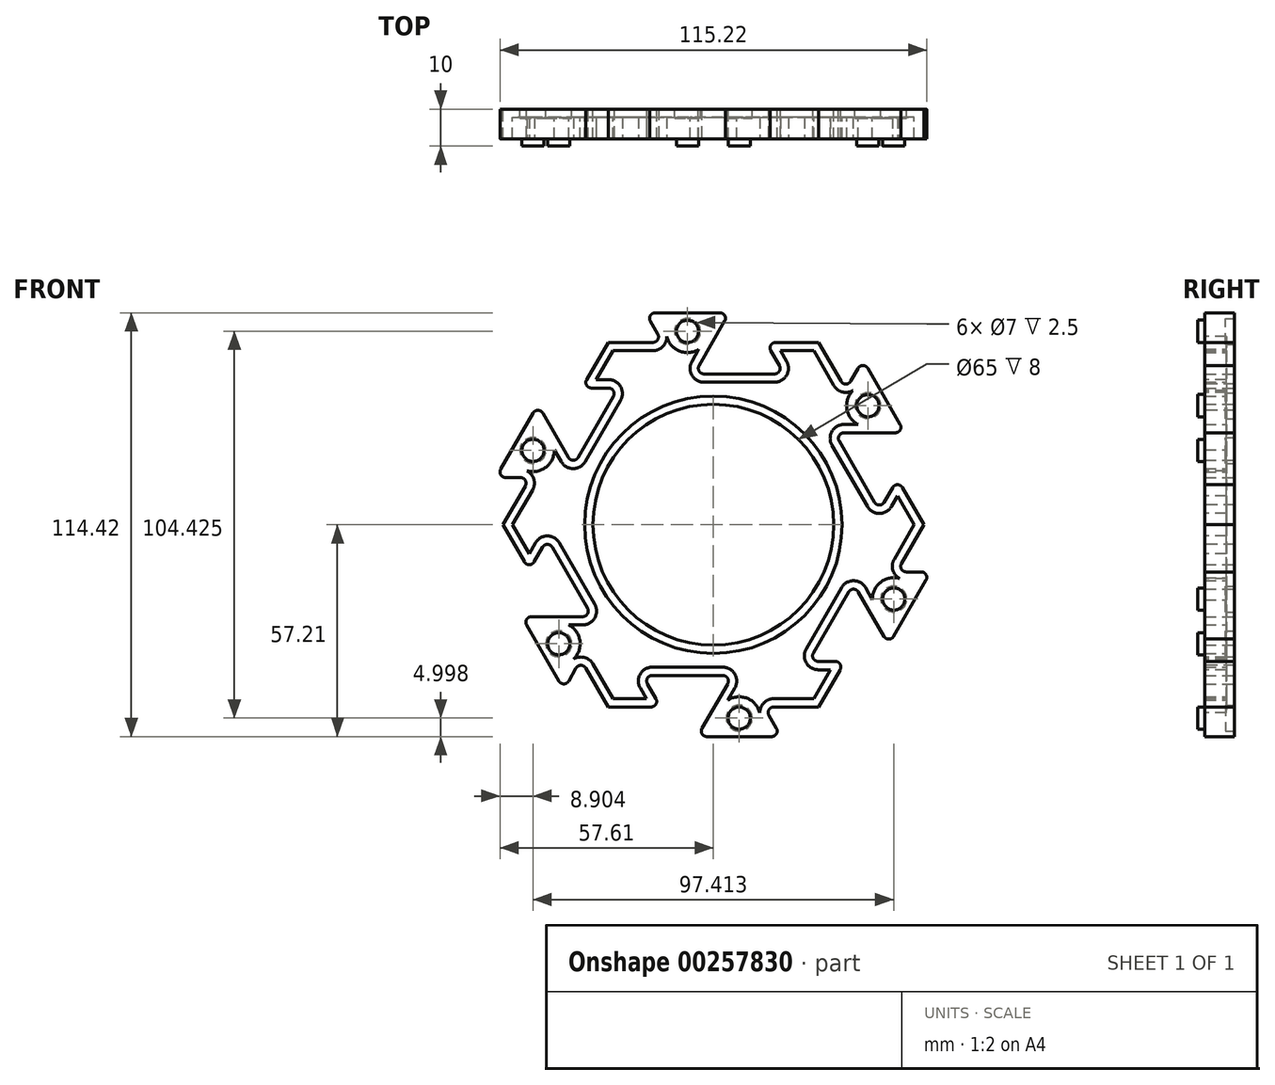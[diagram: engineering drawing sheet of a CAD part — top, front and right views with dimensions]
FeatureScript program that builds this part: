
annotation { "Feature Type Name" : "Feature", "Feature Type Description" : "" }
export const myFeature = defineFeature(function(context is Context, id is Id, definition is map)
    precondition{}
    {
        {
            var Q0;
            Q0=qCreatedBy(makeId("Front.planeOp"),FACE);
            var sketch = newSketch(context, id + "F0", { "sketchPlane" : qUnion([Q0])});
            skLineSegment(sketch, "E0.0", {"start": v(-28.41, 49.21) * mm, "end": v(-13.7, 49.21) * mm});
            skPoint(sketch, "E0.0.midPoint", {"position": v(0, 49.21) * mm});
            skPoint(sketch, "E1", {"position": v(-13.7, 49.21) * mm});
            skPoint(sketch, "E2", {"position": v(-0.25, 49.21) * mm});
            skPoint(sketch, "E3", {"position": v(14.2, 49.21) * mm});
            skPoint(sketch, "E4", {"position": v(-5.16, 40.71) * mm});
            skLineSegment(sketch, "E5", {"start": v(14.2, 49.21) * mm, "end": v(19.11, 40.71) * mm, "construction": true});
            skLineSegment(sketch, "E6", {"start": v(-13.7, 49.21) * mm, "end": v(-18.33, 57.21) * mm, "construction": true});
            skPoint(sketch, "E7", {"position": v(-18.33, 57.21) * mm});
            skPoint(sketch, "E8", {"position": v(4.37, 57.21) * mm});
            skPoint(sketch, "E9", {"position": v(19.11, 40.71) * mm});
            skLineSegment(sketch, "E10.trimOffspring", {"start": v(-0.25, 49.21) * mm, "end": v(0, 49.21) * mm});
            skLineSegment(sketch, "E11.trimOffspring", {"start": v(14.2, 49.21) * mm, "end": v(28.41, 49.21) * mm});
            skLineSegment(sketch, "E12", {"start": v(-13.7, 49.21) * mm, "end": v(-18.33, 57.21) * mm});
            skLineSegment(sketch, "E13", {"start": v(4.37, 57.21) * mm, "end": v(-0.25, 49.21) * mm});
            skLineSegment(sketch, "E14", {"start": v(-5.16, 40.71) * mm, "end": v(-0.25, 49.21) * mm});
            skLineSegment(sketch, "E15", {"start": v(-5.16, 40.71) * mm, "end": v(19.11, 40.71) * mm});
            skLineSegment(sketch, "E16", {"start": v(19.11, 40.71) * mm, "end": v(14.2, 49.21) * mm});
            skLineSegment(sketch, "E17", {"start": v(-18.33, 57.21) * mm, "end": v(4.37, 57.21) * mm});
            skLineSegment(sketch, "E18", {"start": v(-28.41, 49.21) * mm, "end": v(-16.75, 29.01) * mm});
            skLineSegment(sketch, "E19", {"start": v(16.75, 29.01) * mm, "end": v(28.41, 49.21) * mm});
            skPoint(sketch, "E20", {"position": v(0, 0) * mm});
            skLineSegment(sketch, "E21", {"start": v(-13.7, 49.21) * mm, "end": v(-0.25, 49.21) * mm, "construction": true});
            skArc(sketch, "E22", {"start": v(16.25, 28.15) * mm, "mid": v(0, 32.5) * mm, "end": v(-16.25, 28.15) * mm});
            skPoint(sketch, "E23", {"position": v(-16.75, 29.01) * mm});
            skPoint(sketch, "E24", {"position": v(14.65, 29.01) * mm});
            skLineSegment(sketch, "E25", {"start": v(-16.75, 29.01) * mm, "end": v(0, 0) * mm, "construction": true});
            skLineSegment(sketch, "E26", {"start": v(0, 0) * mm, "end": v(16.75, 29.01) * mm, "construction": true});
            skLineSegment(sketch, "E27", {"start": v(-16.75, 29.01) * mm, "end": v(-16.25, 28.15) * mm});
            skLineSegment(sketch, "E28", {"start": v(16.75, 29.01) * mm, "end": v(16.25, 28.15) * mm});
            skSolve(sketch);
        }
        {
            var Q0;
            Q0=qCreatedBy(makeId("Right.planeOp"),FACE);
            var sketch = newSketch(context, id + "F1", { "sketchPlane" : qUnion([Q0])});
            skLineSegment(sketch, "E29", {"start": v(0, 0) * mm, "end": v(-16.4, 0) * mm, "construction": true});
            skSolve(sketch);
        }
        {
            var Q0;
            Q0=makeQuery(id+"F0.imprint","IMPRINT",FACE,{"disambiguationData":[TD([[makeQuery(id+"F0.imprint","IMPRINT",EDGE,{"derivedFrom":sQuery(id+"F0.wireOp",EDGE,"E0.0")}),-1.0]])]});
            extrude(context, id + "F2", {"entities" : qUnion([Q0]), "depth" : 8 * mm});
        }
        {
            var Q0;
            {var subQ0=makeQuery(id+"F2.opExtrude","CAP_FACE",FACE,{"disambiguationData":[OSD([sQuery(id+"F0.wireOp",EDGE,"Ghvy13B3-qNFz-JgCi-f515-eY6BPN7KZuCC"),sQuery(id+"F0.wireOp",EDGE,"E0.0"),sQuery(id+"F0.wireOp",EDGE,"E11.trimOffspring"),sQuery(id+"F0.wireOp",EDGE,"E12"),sQuery(id+"F0.wireOp",EDGE,"E13"),sQuery(id+"F0.wireOp",EDGE,"E14"),sQuery(id+"F0.wireOp",EDGE,"E15"),sQuery(id+"F0.wireOp",EDGE,"E16"),sQuery(id+"F0.wireOp",EDGE,"E17"),sQuery(id+"F0.wireOp",EDGE,"E18"),sQuery(id+"F0.wireOp",EDGE,"E19")])],"isStart":false});Q0=makeQuery(id+"F12.opBoolean","MERGE",FACE,{"derivedFrom":[subQ0,makeQuery(id+"F7.opPattern","COPY",FACE,{"derivedFrom":subQ0,"instanceName":"1"}),makeQuery(id+"F8.opPattern","COPY",FACE,{"derivedFrom":subQ0,"instanceName":"1"}),makeQuery(id+"F9.opPattern","COPY",FACE,{"derivedFrom":subQ0,"instanceName":"1"}),makeQuery(id+"F10.opPattern","COPY",FACE,{"derivedFrom":subQ0,"instanceName":"1"}),makeQuery(id+"F11.opPattern","COPY",FACE,{"derivedFrom":subQ0,"instanceName":"1"})]});}
            var sketch = newSketch(context, id + "F3", { "sketchPlane" : qUnion([Q0])});
            skLineSegment(sketch, "E30", {"start": v(-13.65, 49.21) * mm, "end": v(-0.25, 49.21) * mm, "construction": true});
            skLineSegment(sketch, "E31", {"start": v(-6.98, 57.21) * mm, "end": v(-6.98, 49.21) * mm, "construction": true});
            skPoint(sketch, "E32", {"position": v(-6.98, 52.21) * mm});
            skCircle(sketch, "E33", {"center": v(-6.98, 52.21) * mm, "radius": 3 * mm});
            skSolve(sketch);
        }
        {
            var Q0;
            Q0=makeQuery(id+"F3.imprint","IMPRINT",FACE,{"disambiguationData":[TD([[makeQuery(id+"F3.imprint","IMPRINT",EDGE,{"derivedFrom":sQuery(id+"F3.wireOp",EDGE,"E33")}),1.0]])]});
            extrude(context, id + "F4", {"entities" : qUnion([Q0]), "operationType" : NewBodyOperationType.ADD, "depth" : 2 * mm});
        }
        {
            var Q0;
            Q0=qCreatedBy(makeId("Front.planeOp"),FACE);
            var sketch = newSketch(context, id + "F5", { "sketchPlane" : qUnion([Q0])});
            skPoint(sketch, "E34.0", {"position": v(-6.98, 52.21) * mm});
            skCircle(sketch, "E35", {"center": v(-6.98, 52.21) * mm, "radius": 3.5 * mm});
            skSolve(sketch);
        }
        {
            var Q0;
            Q0=makeQuery(id+"F5.imprint","IMPRINT",FACE,{"disambiguationData":[TD([[makeQuery(id+"F5.imprint","IMPRINT",EDGE,{"derivedFrom":sQuery(id+"F5.wireOp",EDGE,"E35")}),1.0]])]});
            var Q1;
            Q1=sQuery(id+"F5.wireOp",EDGE,"E35");
            extrude(context, id + "F6", {"entities" : qUnion([Q0]), "operationType" : NewBodyOperationType.REMOVE, "surfaceEntities" : qUnion([Q1]), "depth" : 2.5 * mm});
        }
        {
            var Q0;
            Q0=makeQuery(id+"F2.opExtrude","SWEPT_BODY",BODY,{"disambiguationData":[OSD([sQuery(id+"F0.wireOp",EDGE,"Ghvy13B3-qNFz-JgCi-f515-eY6BPN7KZuCC"),sQuery(id+"F0.wireOp",EDGE,"E0.0"),sQuery(id+"F0.wireOp",EDGE,"E11.trimOffspring"),sQuery(id+"F0.wireOp",EDGE,"E12"),sQuery(id+"F0.wireOp",EDGE,"E13"),sQuery(id+"F0.wireOp",EDGE,"E14"),sQuery(id+"F0.wireOp",EDGE,"E15"),sQuery(id+"F0.wireOp",EDGE,"E16"),sQuery(id+"F0.wireOp",EDGE,"E17"),sQuery(id+"F0.wireOp",EDGE,"E18"),sQuery(id+"F0.wireOp",EDGE,"E19")])]});
            var Q1;
            Q1=sQuery(id+"F1.wireOp",EDGE,"E29");
            transform(context, id + "F7", {"entities" : qUnion([Q0]), "transformType" : TransformType.ROTATION, "transformAxis" : qUnion([Q1]), "angle" : 60 * degree, "makeCopy" : true});
        }
        {
            var Q0;
            Q0=makeQuery(id+"F2.opExtrude","SWEPT_BODY",BODY,{"disambiguationData":[OSD([sQuery(id+"F0.wireOp",EDGE,"Ghvy13B3-qNFz-JgCi-f515-eY6BPN7KZuCC"),sQuery(id+"F0.wireOp",EDGE,"E0.0"),sQuery(id+"F0.wireOp",EDGE,"E11.trimOffspring"),sQuery(id+"F0.wireOp",EDGE,"E12"),sQuery(id+"F0.wireOp",EDGE,"E13"),sQuery(id+"F0.wireOp",EDGE,"E14"),sQuery(id+"F0.wireOp",EDGE,"E15"),sQuery(id+"F0.wireOp",EDGE,"E16"),sQuery(id+"F0.wireOp",EDGE,"E17"),sQuery(id+"F0.wireOp",EDGE,"E18"),sQuery(id+"F0.wireOp",EDGE,"E19")])]});
            var Q1;
            Q1=sQuery(id+"F1.wireOp",EDGE,"E29");
            transform(context, id + "F8", {"entities" : qUnion([Q0]), "transformType" : TransformType.ROTATION, "transformAxis" : qUnion([Q1]), "angle" : 120 * degree, "makeCopy" : true});
        }
        {
            var Q0;
            Q0=makeQuery(id+"F2.opExtrude","SWEPT_BODY",BODY,{"disambiguationData":[OSD([sQuery(id+"F0.wireOp",EDGE,"Ghvy13B3-qNFz-JgCi-f515-eY6BPN7KZuCC"),sQuery(id+"F0.wireOp",EDGE,"E0.0"),sQuery(id+"F0.wireOp",EDGE,"E11.trimOffspring"),sQuery(id+"F0.wireOp",EDGE,"E12"),sQuery(id+"F0.wireOp",EDGE,"E13"),sQuery(id+"F0.wireOp",EDGE,"E14"),sQuery(id+"F0.wireOp",EDGE,"E15"),sQuery(id+"F0.wireOp",EDGE,"E16"),sQuery(id+"F0.wireOp",EDGE,"E17"),sQuery(id+"F0.wireOp",EDGE,"E18"),sQuery(id+"F0.wireOp",EDGE,"E19")])]});
            var Q1;
            Q1=sQuery(id+"F1.wireOp",EDGE,"E29");
            transform(context, id + "F9", {"entities" : qUnion([Q0]), "transformType" : TransformType.ROTATION, "transformAxis" : qUnion([Q1]), "angle" : 180 * degree, "makeCopy" : true});
        }
        {
            var Q0;
            Q0=makeQuery(id+"F2.opExtrude","SWEPT_BODY",BODY,{"disambiguationData":[OSD([sQuery(id+"F0.wireOp",EDGE,"Ghvy13B3-qNFz-JgCi-f515-eY6BPN7KZuCC"),sQuery(id+"F0.wireOp",EDGE,"E0.0"),sQuery(id+"F0.wireOp",EDGE,"E11.trimOffspring"),sQuery(id+"F0.wireOp",EDGE,"E12"),sQuery(id+"F0.wireOp",EDGE,"E13"),sQuery(id+"F0.wireOp",EDGE,"E14"),sQuery(id+"F0.wireOp",EDGE,"E15"),sQuery(id+"F0.wireOp",EDGE,"E16"),sQuery(id+"F0.wireOp",EDGE,"E17"),sQuery(id+"F0.wireOp",EDGE,"E18"),sQuery(id+"F0.wireOp",EDGE,"E19")])]});
            var Q1;
            Q1=sQuery(id+"F1.wireOp",EDGE,"E29");
            transform(context, id + "F10", {"entities" : qUnion([Q0]), "transformType" : TransformType.ROTATION, "transformAxis" : qUnion([Q1]), "angle" : 240 * degree, "makeCopy" : true});
        }
        {
            var Q0;
            Q0=makeQuery(id+"F2.opExtrude","SWEPT_BODY",BODY,{"disambiguationData":[OSD([sQuery(id+"F0.wireOp",EDGE,"Ghvy13B3-qNFz-JgCi-f515-eY6BPN7KZuCC"),sQuery(id+"F0.wireOp",EDGE,"E0.0"),sQuery(id+"F0.wireOp",EDGE,"E11.trimOffspring"),sQuery(id+"F0.wireOp",EDGE,"E12"),sQuery(id+"F0.wireOp",EDGE,"E13"),sQuery(id+"F0.wireOp",EDGE,"E14"),sQuery(id+"F0.wireOp",EDGE,"E15"),sQuery(id+"F0.wireOp",EDGE,"E16"),sQuery(id+"F0.wireOp",EDGE,"E17"),sQuery(id+"F0.wireOp",EDGE,"E18"),sQuery(id+"F0.wireOp",EDGE,"E19")])]});
            var Q1;
            Q1=sQuery(id+"F1.wireOp",EDGE,"E29");
            transform(context, id + "F11", {"entities" : qUnion([Q0]), "transformType" : TransformType.ROTATION, "transformAxis" : qUnion([Q1]), "angle" : 300 * degree, "makeCopy" : true});
        }
        {
            var Q0;
            Q0=makeQuery(id+"F2.opExtrude","SWEPT_BODY",BODY,{"disambiguationData":[OSD([sQuery(id+"F0.wireOp",EDGE,"Ghvy13B3-qNFz-JgCi-f515-eY6BPN7KZuCC"),sQuery(id+"F0.wireOp",EDGE,"E0.0"),sQuery(id+"F0.wireOp",EDGE,"E11.trimOffspring"),sQuery(id+"F0.wireOp",EDGE,"E12"),sQuery(id+"F0.wireOp",EDGE,"E13"),sQuery(id+"F0.wireOp",EDGE,"E14"),sQuery(id+"F0.wireOp",EDGE,"E15"),sQuery(id+"F0.wireOp",EDGE,"E16"),sQuery(id+"F0.wireOp",EDGE,"E17"),sQuery(id+"F0.wireOp",EDGE,"E18"),sQuery(id+"F0.wireOp",EDGE,"E19")])]});
            var Q1;
            Q1=makeQuery(id+"F7.opPattern","COPY",BODY,{"derivedFrom":makeQuery(id+"F2.opExtrude","SWEPT_BODY",BODY,{"disambiguationData":[OSD([sQuery(id+"F0.wireOp",EDGE,"Ghvy13B3-qNFz-JgCi-f515-eY6BPN7KZuCC"),sQuery(id+"F0.wireOp",EDGE,"E0.0"),sQuery(id+"F0.wireOp",EDGE,"E11.trimOffspring"),sQuery(id+"F0.wireOp",EDGE,"E12"),sQuery(id+"F0.wireOp",EDGE,"E13"),sQuery(id+"F0.wireOp",EDGE,"E14"),sQuery(id+"F0.wireOp",EDGE,"E15"),sQuery(id+"F0.wireOp",EDGE,"E16"),sQuery(id+"F0.wireOp",EDGE,"E17"),sQuery(id+"F0.wireOp",EDGE,"E18"),sQuery(id+"F0.wireOp",EDGE,"E19")])]}),"instanceName":"1"});
            var Q2;
            Q2=makeQuery(id+"F8.opPattern","COPY",BODY,{"derivedFrom":makeQuery(id+"F2.opExtrude","SWEPT_BODY",BODY,{"disambiguationData":[OSD([sQuery(id+"F0.wireOp",EDGE,"Ghvy13B3-qNFz-JgCi-f515-eY6BPN7KZuCC"),sQuery(id+"F0.wireOp",EDGE,"E0.0"),sQuery(id+"F0.wireOp",EDGE,"E11.trimOffspring"),sQuery(id+"F0.wireOp",EDGE,"E12"),sQuery(id+"F0.wireOp",EDGE,"E13"),sQuery(id+"F0.wireOp",EDGE,"E14"),sQuery(id+"F0.wireOp",EDGE,"E15"),sQuery(id+"F0.wireOp",EDGE,"E16"),sQuery(id+"F0.wireOp",EDGE,"E17"),sQuery(id+"F0.wireOp",EDGE,"E18"),sQuery(id+"F0.wireOp",EDGE,"E19")])]}),"instanceName":"1"});
            var Q3;
            Q3=makeQuery(id+"F9.opPattern","COPY",BODY,{"derivedFrom":makeQuery(id+"F2.opExtrude","SWEPT_BODY",BODY,{"disambiguationData":[OSD([sQuery(id+"F0.wireOp",EDGE,"Ghvy13B3-qNFz-JgCi-f515-eY6BPN7KZuCC"),sQuery(id+"F0.wireOp",EDGE,"E0.0"),sQuery(id+"F0.wireOp",EDGE,"E11.trimOffspring"),sQuery(id+"F0.wireOp",EDGE,"E12"),sQuery(id+"F0.wireOp",EDGE,"E13"),sQuery(id+"F0.wireOp",EDGE,"E14"),sQuery(id+"F0.wireOp",EDGE,"E15"),sQuery(id+"F0.wireOp",EDGE,"E16"),sQuery(id+"F0.wireOp",EDGE,"E17"),sQuery(id+"F0.wireOp",EDGE,"E18"),sQuery(id+"F0.wireOp",EDGE,"E19")])]}),"instanceName":"1"});
            var Q4;
            Q4=makeQuery(id+"F10.opPattern","COPY",BODY,{"derivedFrom":makeQuery(id+"F2.opExtrude","SWEPT_BODY",BODY,{"disambiguationData":[OSD([sQuery(id+"F0.wireOp",EDGE,"Ghvy13B3-qNFz-JgCi-f515-eY6BPN7KZuCC"),sQuery(id+"F0.wireOp",EDGE,"E0.0"),sQuery(id+"F0.wireOp",EDGE,"E11.trimOffspring"),sQuery(id+"F0.wireOp",EDGE,"E12"),sQuery(id+"F0.wireOp",EDGE,"E13"),sQuery(id+"F0.wireOp",EDGE,"E14"),sQuery(id+"F0.wireOp",EDGE,"E15"),sQuery(id+"F0.wireOp",EDGE,"E16"),sQuery(id+"F0.wireOp",EDGE,"E17"),sQuery(id+"F0.wireOp",EDGE,"E18"),sQuery(id+"F0.wireOp",EDGE,"E19")])]}),"instanceName":"1"});
            var Q5;
            Q5=makeQuery(id+"F11.opPattern","COPY",BODY,{"derivedFrom":makeQuery(id+"F2.opExtrude","SWEPT_BODY",BODY,{"disambiguationData":[OSD([sQuery(id+"F0.wireOp",EDGE,"Ghvy13B3-qNFz-JgCi-f515-eY6BPN7KZuCC"),sQuery(id+"F0.wireOp",EDGE,"E0.0"),sQuery(id+"F0.wireOp",EDGE,"E11.trimOffspring"),sQuery(id+"F0.wireOp",EDGE,"E12"),sQuery(id+"F0.wireOp",EDGE,"E13"),sQuery(id+"F0.wireOp",EDGE,"E14"),sQuery(id+"F0.wireOp",EDGE,"E15"),sQuery(id+"F0.wireOp",EDGE,"E16"),sQuery(id+"F0.wireOp",EDGE,"E17"),sQuery(id+"F0.wireOp",EDGE,"E18"),sQuery(id+"F0.wireOp",EDGE,"E19")])]}),"instanceName":"1"});
            booleanBodies(context, id + "F12", {"operationType" : BooleanOperationType.UNION, "tools" : qUnion([Q0, Q1, Q2, Q3, Q4, Q5])});
        }
        {
            var Q0;
            Q0=makeQuery(id+"F7.opPattern","COPY",EDGE,{"derivedFrom":makeQuery(id+"F2.opExtrude","SWEPT_EDGE",EDGE,{"disambiguationData":[OSD([sQuery(id+"F0.wireOp",EDGE,"E11.trimOffspring"),sQuery(id+"F0.wireOp",EDGE,"E16")])]}),"instanceName":"1"});
            var Q1;
            Q1=makeQuery(id+"F7.opPattern","COPY",EDGE,{"derivedFrom":makeQuery(id+"F2.opExtrude","SWEPT_EDGE",EDGE,{"disambiguationData":[OSD([sQuery(id+"F0.wireOp",EDGE,"E13"),sQuery(id+"F0.wireOp",EDGE,"E17")])]}),"instanceName":"1"});
            var Q2;
            Q2=makeQuery(id+"F7.opPattern","COPY",EDGE,{"derivedFrom":makeQuery(id+"F2.opExtrude","SWEPT_EDGE",EDGE,{"disambiguationData":[OSD([sQuery(id+"F0.wireOp",EDGE,"E12"),sQuery(id+"F0.wireOp",EDGE,"E17")])]}),"instanceName":"1"});
            var Q3;
            Q3=makeQuery(id+"F2.opExtrude","SWEPT_EDGE",EDGE,{"disambiguationData":[OSD([sQuery(id+"F0.wireOp",EDGE,"E12"),sQuery(id+"F0.wireOp",EDGE,"E17")])]});
            var Q4;
            Q4=makeQuery(id+"F2.opExtrude","SWEPT_EDGE",EDGE,{"disambiguationData":[OSD([sQuery(id+"F0.wireOp",EDGE,"E11.trimOffspring"),sQuery(id+"F0.wireOp",EDGE,"E16")])]});
            var Q5;
            Q5=makeQuery(id+"F11.opPattern","COPY",EDGE,{"derivedFrom":makeQuery(id+"F2.opExtrude","SWEPT_EDGE",EDGE,{"disambiguationData":[OSD([sQuery(id+"F0.wireOp",EDGE,"E12"),sQuery(id+"F0.wireOp",EDGE,"E17")])]}),"instanceName":"1"});
            var Q6;
            Q6=makeQuery(id+"F11.opPattern","COPY",EDGE,{"derivedFrom":makeQuery(id+"F2.opExtrude","SWEPT_EDGE",EDGE,{"disambiguationData":[OSD([sQuery(id+"F0.wireOp",EDGE,"E11.trimOffspring"),sQuery(id+"F0.wireOp",EDGE,"E16")])]}),"instanceName":"1"});
            var Q7;
            Q7=makeQuery(id+"F10.opPattern","COPY",EDGE,{"derivedFrom":makeQuery(id+"F2.opExtrude","SWEPT_EDGE",EDGE,{"disambiguationData":[OSD([sQuery(id+"F0.wireOp",EDGE,"E13"),sQuery(id+"F0.wireOp",EDGE,"E17")])]}),"instanceName":"1"});
            var Q8;
            Q8=makeQuery(id+"F9.opPattern","COPY",EDGE,{"derivedFrom":makeQuery(id+"F2.opExtrude","SWEPT_EDGE",EDGE,{"disambiguationData":[OSD([sQuery(id+"F0.wireOp",EDGE,"E13"),sQuery(id+"F0.wireOp",EDGE,"E17")])]}),"instanceName":"1"});
            var Q9;
            Q9=makeQuery(id+"F8.opPattern","COPY",EDGE,{"derivedFrom":makeQuery(id+"F2.opExtrude","SWEPT_EDGE",EDGE,{"disambiguationData":[OSD([sQuery(id+"F0.wireOp",EDGE,"E12"),sQuery(id+"F0.wireOp",EDGE,"E17")])]}),"instanceName":"1"});
            var Q10;
            Q10=makeQuery(id+"F8.opPattern","COPY",EDGE,{"derivedFrom":makeQuery(id+"F2.opExtrude","SWEPT_EDGE",EDGE,{"disambiguationData":[OSD([sQuery(id+"F0.wireOp",EDGE,"E13"),sQuery(id+"F0.wireOp",EDGE,"E17")])]}),"instanceName":"1"});
            var Q11;
            Q11=makeQuery(id+"F8.opPattern","COPY",EDGE,{"derivedFrom":makeQuery(id+"F2.opExtrude","SWEPT_EDGE",EDGE,{"disambiguationData":[OSD([sQuery(id+"F0.wireOp",EDGE,"E11.trimOffspring"),sQuery(id+"F0.wireOp",EDGE,"E16")])]}),"instanceName":"1"});
            var Q12;
            Q12=makeQuery(id+"F2.opExtrude","SWEPT_EDGE",EDGE,{"disambiguationData":[OSD([sQuery(id+"F0.wireOp",EDGE,"E13"),sQuery(id+"F0.wireOp",EDGE,"E17")])]});
            var Q13;
            Q13=makeQuery(id+"F11.opPattern","COPY",EDGE,{"derivedFrom":makeQuery(id+"F2.opExtrude","SWEPT_EDGE",EDGE,{"disambiguationData":[OSD([sQuery(id+"F0.wireOp",EDGE,"E13"),sQuery(id+"F0.wireOp",EDGE,"E17")])]}),"instanceName":"1"});
            var Q14;
            Q14=makeQuery(id+"F10.opPattern","COPY",EDGE,{"derivedFrom":makeQuery(id+"F2.opExtrude","SWEPT_EDGE",EDGE,{"disambiguationData":[OSD([sQuery(id+"F0.wireOp",EDGE,"E12"),sQuery(id+"F0.wireOp",EDGE,"E17")])]}),"instanceName":"1"});
            var Q15;
            Q15=makeQuery(id+"F10.opPattern","COPY",EDGE,{"derivedFrom":makeQuery(id+"F2.opExtrude","SWEPT_EDGE",EDGE,{"disambiguationData":[OSD([sQuery(id+"F0.wireOp",EDGE,"E11.trimOffspring"),sQuery(id+"F0.wireOp",EDGE,"E16")])]}),"instanceName":"1"});
            var Q16;
            Q16=makeQuery(id+"F9.opPattern","COPY",EDGE,{"derivedFrom":makeQuery(id+"F2.opExtrude","SWEPT_EDGE",EDGE,{"disambiguationData":[OSD([sQuery(id+"F0.wireOp",EDGE,"E12"),sQuery(id+"F0.wireOp",EDGE,"E17")])]}),"instanceName":"1"});
            var Q17;
            Q17=makeQuery(id+"F9.opPattern","COPY",EDGE,{"derivedFrom":makeQuery(id+"F2.opExtrude","SWEPT_EDGE",EDGE,{"disambiguationData":[OSD([sQuery(id+"F0.wireOp",EDGE,"E11.trimOffspring"),sQuery(id+"F0.wireOp",EDGE,"E16")])]}),"instanceName":"1"});
            var Q18;
            Q18=makeQuery(id+"F7.opPattern","COPY",EDGE,{"derivedFrom":makeQuery(id+"F2.opExtrude","SWEPT_EDGE",EDGE,{"disambiguationData":[OSD([sQuery(id+"F0.wireOp",EDGE,"E14"),sQuery(id+"F0.wireOp",EDGE,"E15")])]}),"instanceName":"1"});
            var Q19;
            Q19=makeQuery(id+"F11.opPattern","COPY",EDGE,{"derivedFrom":makeQuery(id+"F2.opExtrude","SWEPT_EDGE",EDGE,{"disambiguationData":[OSD([sQuery(id+"F0.wireOp",EDGE,"E15"),sQuery(id+"F0.wireOp",EDGE,"E16")])]}),"instanceName":"1"});
            var Q20;
            Q20=makeQuery(id+"F11.opPattern","COPY",EDGE,{"derivedFrom":makeQuery(id+"F2.opExtrude","SWEPT_EDGE",EDGE,{"disambiguationData":[OSD([sQuery(id+"F0.wireOp",EDGE,"E0.0"),sQuery(id+"F0.wireOp",EDGE,"E12")])]}),"instanceName":"1"});
            var Q21;
            Q21=makeQuery(id+"F2.opExtrude","SWEPT_EDGE",EDGE,{"disambiguationData":[OSD([sQuery(id+"F0.wireOp",EDGE,"E14"),sQuery(id+"F0.wireOp",EDGE,"E15")])]});
            var Q22;
            Q22=makeQuery(id+"F2.opExtrude","SWEPT_EDGE",EDGE,{"disambiguationData":[OSD([sQuery(id+"F0.wireOp",EDGE,"E15"),sQuery(id+"F0.wireOp",EDGE,"E16")])]});
            var Q23;
            Q23=makeQuery(id+"F7.opPattern","COPY",EDGE,{"derivedFrom":makeQuery(id+"F2.opExtrude","SWEPT_EDGE",EDGE,{"disambiguationData":[OSD([sQuery(id+"F0.wireOp",EDGE,"E15"),sQuery(id+"F0.wireOp",EDGE,"E16")])]}),"instanceName":"1"});
            var Q24;
            Q24=makeQuery(id+"F9.opPattern","COPY",EDGE,{"derivedFrom":makeQuery(id+"F2.opExtrude","SWEPT_EDGE",EDGE,{"disambiguationData":[OSD([sQuery(id+"F0.wireOp",EDGE,"E14"),sQuery(id+"F0.wireOp",EDGE,"E15")])]}),"instanceName":"1"});
            var Q25;
            Q25=makeQuery(id+"F8.opPattern","COPY",EDGE,{"derivedFrom":makeQuery(id+"F2.opExtrude","SWEPT_EDGE",EDGE,{"disambiguationData":[OSD([sQuery(id+"F0.wireOp",EDGE,"E15"),sQuery(id+"F0.wireOp",EDGE,"E16")])]}),"instanceName":"1"});
            var Q26;
            Q26=makeQuery(id+"F8.opPattern","COPY",EDGE,{"derivedFrom":makeQuery(id+"F2.opExtrude","SWEPT_EDGE",EDGE,{"disambiguationData":[OSD([sQuery(id+"F0.wireOp",EDGE,"E14"),sQuery(id+"F0.wireOp",EDGE,"E15")])]}),"instanceName":"1"});
            var Q27;
            Q27=makeQuery(id+"F9.opPattern","COPY",EDGE,{"derivedFrom":makeQuery(id+"F2.opExtrude","SWEPT_EDGE",EDGE,{"disambiguationData":[OSD([sQuery(id+"F0.wireOp",EDGE,"E15"),sQuery(id+"F0.wireOp",EDGE,"E16")])]}),"instanceName":"1"});
            var Q28;
            Q28=makeQuery(id+"F9.opPattern","COPY",EDGE,{"derivedFrom":makeQuery(id+"F2.opExtrude","SWEPT_EDGE",EDGE,{"disambiguationData":[OSD([sQuery(id+"F0.wireOp",EDGE,"E0.0"),sQuery(id+"F0.wireOp",EDGE,"E12")])]}),"instanceName":"1"});
            var Q29;
            Q29=makeQuery(id+"F11.opPattern","COPY",EDGE,{"derivedFrom":makeQuery(id+"F2.opExtrude","SWEPT_EDGE",EDGE,{"disambiguationData":[OSD([sQuery(id+"F0.wireOp",EDGE,"E14"),sQuery(id+"F0.wireOp",EDGE,"E15")])]}),"instanceName":"1"});
            var Q30;
            Q30=makeQuery(id+"F2.opExtrude","SWEPT_EDGE",EDGE,{"disambiguationData":[OSD([sQuery(id+"F0.wireOp",EDGE,"E0.0"),sQuery(id+"F0.wireOp",EDGE,"E12")])]});
            var Q31;
            Q31=makeQuery(id+"F10.opPattern","COPY",EDGE,{"derivedFrom":makeQuery(id+"F2.opExtrude","SWEPT_EDGE",EDGE,{"disambiguationData":[OSD([sQuery(id+"F0.wireOp",EDGE,"E15"),sQuery(id+"F0.wireOp",EDGE,"E16")])]}),"instanceName":"1"});
            var Q32;
            Q32=makeQuery(id+"F10.opPattern","COPY",EDGE,{"derivedFrom":makeQuery(id+"F2.opExtrude","SWEPT_EDGE",EDGE,{"disambiguationData":[OSD([sQuery(id+"F0.wireOp",EDGE,"E14"),sQuery(id+"F0.wireOp",EDGE,"E15")])]}),"instanceName":"1"});
            var Q33;
            Q33=makeQuery(id+"F10.opPattern","COPY",EDGE,{"derivedFrom":makeQuery(id+"F2.opExtrude","SWEPT_EDGE",EDGE,{"disambiguationData":[OSD([sQuery(id+"F0.wireOp",EDGE,"E0.0"),sQuery(id+"F0.wireOp",EDGE,"E12")])]}),"instanceName":"1"});
            var Q34;
            Q34=makeQuery(id+"F8.opPattern","COPY",EDGE,{"derivedFrom":makeQuery(id+"F2.opExtrude","SWEPT_EDGE",EDGE,{"disambiguationData":[OSD([sQuery(id+"F0.wireOp",EDGE,"E0.0"),sQuery(id+"F0.wireOp",EDGE,"E12")])]}),"instanceName":"1"});
            var Q35;
            Q35=makeQuery(id+"F7.opPattern","COPY",EDGE,{"derivedFrom":makeQuery(id+"F2.opExtrude","SWEPT_EDGE",EDGE,{"disambiguationData":[OSD([sQuery(id+"F0.wireOp",EDGE,"E0.0"),sQuery(id+"F0.wireOp",EDGE,"E12")])]}),"instanceName":"1"});
            fillet(context, id + "F13", {"entities" : qUnion([Q0, Q1, Q2, Q3, Q4, Q5, Q6, Q7, Q8, Q9, Q10, Q11, Q12, Q13, Q14, Q15, Q16, Q17, Q18, Q19, Q20, Q21, Q22, Q23, Q24, Q25, Q26, Q27, Q28, Q29, Q30, Q31, Q32, Q33, Q34, Q35]), "radius" : 1.5 * mm, "tangentPropagation" : true, "allowEdgeOverflow" : false});
        }
        {
            var Q0;
            {var subQ0=makeQuery(id+"F2.opExtrude","CAP_FACE",FACE,{"disambiguationData":[OSD([sQuery(id+"F0.wireOp",EDGE,"Ghvy13B3-qNFz-JgCi-f515-eY6BPN7KZuCC"),sQuery(id+"F0.wireOp",EDGE,"E0.0"),sQuery(id+"F0.wireOp",EDGE,"E11.trimOffspring"),sQuery(id+"F0.wireOp",EDGE,"E12"),sQuery(id+"F0.wireOp",EDGE,"E13"),sQuery(id+"F0.wireOp",EDGE,"E14"),sQuery(id+"F0.wireOp",EDGE,"E15"),sQuery(id+"F0.wireOp",EDGE,"E16"),sQuery(id+"F0.wireOp",EDGE,"E17"),sQuery(id+"F0.wireOp",EDGE,"E18"),sQuery(id+"F0.wireOp",EDGE,"E19")])],"isStart":false});Q0=makeQuery(id+"F12.opBoolean","MERGE",FACE,{"derivedFrom":[subQ0,makeQuery(id+"F7.opPattern","COPY",FACE,{"derivedFrom":subQ0,"instanceName":"1"}),makeQuery(id+"F8.opPattern","COPY",FACE,{"derivedFrom":subQ0,"instanceName":"1"}),makeQuery(id+"F9.opPattern","COPY",FACE,{"derivedFrom":subQ0,"instanceName":"1"}),makeQuery(id+"F10.opPattern","COPY",FACE,{"derivedFrom":subQ0,"instanceName":"1"}),makeQuery(id+"F11.opPattern","COPY",FACE,{"derivedFrom":subQ0,"instanceName":"1"})]});}
            var Q1;
            Q1=makeQuery(id+"F2.opExtrude","SWEPT_BODY",BODY,{"disambiguationData":[OSD([sQuery(id+"F0.wireOp",EDGE,"Ghvy13B3-qNFz-JgCi-f515-eY6BPN7KZuCC"),sQuery(id+"F0.wireOp",EDGE,"E0.0"),sQuery(id+"F0.wireOp",EDGE,"E11.trimOffspring"),sQuery(id+"F0.wireOp",EDGE,"E12"),sQuery(id+"F0.wireOp",EDGE,"E13"),sQuery(id+"F0.wireOp",EDGE,"E14"),sQuery(id+"F0.wireOp",EDGE,"E15"),sQuery(id+"F0.wireOp",EDGE,"E16"),sQuery(id+"F0.wireOp",EDGE,"E17"),sQuery(id+"F0.wireOp",EDGE,"E18"),sQuery(id+"F0.wireOp",EDGE,"E19")])]});
            shell(context, id + "F14", {"entities" : qUnion([Q0]), "parts" : qUnion([Q1]), "thickness" : 2.25 * mm});
        }
        {
            var Q0;
            {var subQ0=sQuery(id+"F0.wireOp",EDGE,"E19");var subQ1=sQuery(id+"F0.wireOp",EDGE,"E18");var subQ2=sQuery(id+"F0.wireOp",EDGE,"E17");var subQ3=sQuery(id+"F0.wireOp",EDGE,"E16");var subQ4=sQuery(id+"F0.wireOp",EDGE,"E15");var subQ5=sQuery(id+"F0.wireOp",EDGE,"E14");var subQ6=sQuery(id+"F0.wireOp",EDGE,"E13");var subQ7=sQuery(id+"F0.wireOp",EDGE,"E12");var subQ8=sQuery(id+"F0.wireOp",EDGE,"E11.trimOffspring");var subQ9=sQuery(id+"F0.wireOp",EDGE,"E0.0");var subQ10=sQuery(id+"F0.wireOp",EDGE,"Ghvy13B3-qNFz-JgCi-f515-eY6BPN7KZuCC");var subQ11=makeQuery(id+"F2.opExtrude","CAP_FACE",FACE,{"disambiguationData":[OSD([subQ10,subQ9,subQ8,subQ7,subQ6,subQ5,subQ4,subQ3,subQ2,subQ1,subQ0])],"isStart":true});Q0=makeQuery(id+"F14.opShell","OFFSET_FACE",FACE,{"disambiguationData":[OSD([subQ10,subQ9,subQ8,subQ7,subQ6,subQ5,subQ4,subQ3,subQ2,subQ1,subQ0]),TDD([makeQuery(id+"F12.opBoolean","MERGE",FACE,{"derivedFrom":[subQ11,makeQuery(id+"F7.opPattern","COPY",FACE,{"derivedFrom":subQ11,"instanceName":"1"}),makeQuery(id+"F8.opPattern","COPY",FACE,{"derivedFrom":subQ11,"instanceName":"1"}),makeQuery(id+"F9.opPattern","COPY",FACE,{"derivedFrom":subQ11,"instanceName":"1"}),makeQuery(id+"F10.opPattern","COPY",FACE,{"derivedFrom":subQ11,"instanceName":"1"}),makeQuery(id+"F11.opPattern","COPY",FACE,{"derivedFrom":subQ11,"instanceName":"1"})]})]),OD(0.0)]});}
            var Q1;
            {var subQ0=sQuery(id+"F0.wireOp",EDGE,"E19");var subQ1=sQuery(id+"F0.wireOp",EDGE,"E18");var subQ2=sQuery(id+"F0.wireOp",EDGE,"E17");var subQ3=sQuery(id+"F0.wireOp",EDGE,"E16");var subQ4=sQuery(id+"F0.wireOp",EDGE,"E15");var subQ5=sQuery(id+"F0.wireOp",EDGE,"E14");var subQ6=sQuery(id+"F0.wireOp",EDGE,"E13");var subQ7=sQuery(id+"F0.wireOp",EDGE,"E12");var subQ8=sQuery(id+"F0.wireOp",EDGE,"E11.trimOffspring");var subQ9=sQuery(id+"F0.wireOp",EDGE,"E0.0");var subQ10=sQuery(id+"F0.wireOp",EDGE,"Ghvy13B3-qNFz-JgCi-f515-eY6BPN7KZuCC");var subQ11=makeQuery(id+"F2.opExtrude","CAP_FACE",FACE,{"disambiguationData":[OSD([subQ10,subQ9,subQ8,subQ7,subQ6,subQ5,subQ4,subQ3,subQ2,subQ1,subQ0])],"isStart":true});Q1=makeQuery(id+"F14.opShell","OFFSET_FACE",FACE,{"disambiguationData":[OSD([subQ10,subQ9,subQ8,subQ7,subQ6,subQ5,subQ4,subQ3,subQ2,subQ1,subQ0]),TDD([makeQuery(id+"F12.opBoolean","MERGE",FACE,{"derivedFrom":[subQ11,makeQuery(id+"F7.opPattern","COPY",FACE,{"derivedFrom":subQ11,"instanceName":"1"}),makeQuery(id+"F8.opPattern","COPY",FACE,{"derivedFrom":subQ11,"instanceName":"1"}),makeQuery(id+"F9.opPattern","COPY",FACE,{"derivedFrom":subQ11,"instanceName":"1"}),makeQuery(id+"F10.opPattern","COPY",FACE,{"derivedFrom":subQ11,"instanceName":"1"}),makeQuery(id+"F11.opPattern","COPY",FACE,{"derivedFrom":subQ11,"instanceName":"1"})]})]),OD(1.0)]});}
            var Q2;
            {var subQ0=sQuery(id+"F5.wireOp",EDGE,"E35");Q2=makeQuery(id+"F14.opShell","OFFSET_FACE",FACE,{"disambiguationData":[OSD([subQ0]),TDD([makeQuery(id+"F6.boolean.opBoolean","COPY",FACE,{"derivedFrom":makeQuery(id+"F6.opExtrude","CAP_FACE",FACE,{"disambiguationData":[OSD([subQ0])],"isStart":false})})])]});}
            var Q3;
            {var subQ0=sQuery(id+"F0.wireOp",EDGE,"E19");var subQ1=sQuery(id+"F0.wireOp",EDGE,"E18");var subQ2=sQuery(id+"F0.wireOp",EDGE,"E17");var subQ3=sQuery(id+"F0.wireOp",EDGE,"E16");var subQ4=sQuery(id+"F0.wireOp",EDGE,"E15");var subQ5=sQuery(id+"F0.wireOp",EDGE,"E14");var subQ6=sQuery(id+"F0.wireOp",EDGE,"E13");var subQ7=sQuery(id+"F0.wireOp",EDGE,"E12");var subQ8=sQuery(id+"F0.wireOp",EDGE,"E11.trimOffspring");var subQ9=sQuery(id+"F0.wireOp",EDGE,"E0.0");var subQ10=sQuery(id+"F0.wireOp",EDGE,"Ghvy13B3-qNFz-JgCi-f515-eY6BPN7KZuCC");var subQ11=makeQuery(id+"F2.opExtrude","CAP_FACE",FACE,{"disambiguationData":[OSD([subQ10,subQ9,subQ8,subQ7,subQ6,subQ5,subQ4,subQ3,subQ2,subQ1,subQ0])],"isStart":true});Q3=makeQuery(id+"F14.opShell","OFFSET_FACE",FACE,{"disambiguationData":[OSD([subQ10,subQ9,subQ8,subQ7,subQ6,subQ5,subQ4,subQ3,subQ2,subQ1,subQ0]),TDD([makeQuery(id+"F12.opBoolean","MERGE",FACE,{"derivedFrom":[subQ11,makeQuery(id+"F7.opPattern","COPY",FACE,{"derivedFrom":subQ11,"instanceName":"1"}),makeQuery(id+"F8.opPattern","COPY",FACE,{"derivedFrom":subQ11,"instanceName":"1"}),makeQuery(id+"F9.opPattern","COPY",FACE,{"derivedFrom":subQ11,"instanceName":"1"}),makeQuery(id+"F10.opPattern","COPY",FACE,{"derivedFrom":subQ11,"instanceName":"1"}),makeQuery(id+"F11.opPattern","COPY",FACE,{"derivedFrom":subQ11,"instanceName":"1"})]})]),OD(10.0)]});}
            var Q4;
            {var subQ0=sQuery(id+"F5.wireOp",EDGE,"E35");Q4=makeQuery(id+"F14.opShell","OFFSET_FACE",FACE,{"disambiguationData":[OSD([subQ0]),TDD([makeQuery(id+"F11.opPattern","COPY",FACE,{"derivedFrom":makeQuery(id+"F6.boolean.opBoolean","COPY",FACE,{"derivedFrom":makeQuery(id+"F6.opExtrude","CAP_FACE",FACE,{"disambiguationData":[OSD([subQ0])],"isStart":false})}),"instanceName":"1"})])]});}
            var Q5;
            {var subQ0=sQuery(id+"F0.wireOp",EDGE,"E19");var subQ1=sQuery(id+"F0.wireOp",EDGE,"E18");var subQ2=sQuery(id+"F0.wireOp",EDGE,"E17");var subQ3=sQuery(id+"F0.wireOp",EDGE,"E16");var subQ4=sQuery(id+"F0.wireOp",EDGE,"E15");var subQ5=sQuery(id+"F0.wireOp",EDGE,"E14");var subQ6=sQuery(id+"F0.wireOp",EDGE,"E13");var subQ7=sQuery(id+"F0.wireOp",EDGE,"E12");var subQ8=sQuery(id+"F0.wireOp",EDGE,"E11.trimOffspring");var subQ9=sQuery(id+"F0.wireOp",EDGE,"E0.0");var subQ10=sQuery(id+"F0.wireOp",EDGE,"Ghvy13B3-qNFz-JgCi-f515-eY6BPN7KZuCC");var subQ11=makeQuery(id+"F2.opExtrude","CAP_FACE",FACE,{"disambiguationData":[OSD([subQ10,subQ9,subQ8,subQ7,subQ6,subQ5,subQ4,subQ3,subQ2,subQ1,subQ0])],"isStart":true});Q5=makeQuery(id+"F14.opShell","OFFSET_FACE",FACE,{"disambiguationData":[OSD([subQ10,subQ9,subQ8,subQ7,subQ6,subQ5,subQ4,subQ3,subQ2,subQ1,subQ0]),TDD([makeQuery(id+"F12.opBoolean","MERGE",FACE,{"derivedFrom":[subQ11,makeQuery(id+"F7.opPattern","COPY",FACE,{"derivedFrom":subQ11,"instanceName":"1"}),makeQuery(id+"F8.opPattern","COPY",FACE,{"derivedFrom":subQ11,"instanceName":"1"}),makeQuery(id+"F9.opPattern","COPY",FACE,{"derivedFrom":subQ11,"instanceName":"1"}),makeQuery(id+"F10.opPattern","COPY",FACE,{"derivedFrom":subQ11,"instanceName":"1"}),makeQuery(id+"F11.opPattern","COPY",FACE,{"derivedFrom":subQ11,"instanceName":"1"})]})]),OD(11.0)]});}
            var Q6;
            {var subQ0=sQuery(id+"F0.wireOp",EDGE,"E19");var subQ1=sQuery(id+"F0.wireOp",EDGE,"E18");var subQ2=sQuery(id+"F0.wireOp",EDGE,"E17");var subQ3=sQuery(id+"F0.wireOp",EDGE,"E16");var subQ4=sQuery(id+"F0.wireOp",EDGE,"E15");var subQ5=sQuery(id+"F0.wireOp",EDGE,"E14");var subQ6=sQuery(id+"F0.wireOp",EDGE,"E13");var subQ7=sQuery(id+"F0.wireOp",EDGE,"E12");var subQ8=sQuery(id+"F0.wireOp",EDGE,"E11.trimOffspring");var subQ9=sQuery(id+"F0.wireOp",EDGE,"E0.0");var subQ10=sQuery(id+"F0.wireOp",EDGE,"Ghvy13B3-qNFz-JgCi-f515-eY6BPN7KZuCC");var subQ11=makeQuery(id+"F2.opExtrude","CAP_FACE",FACE,{"disambiguationData":[OSD([subQ10,subQ9,subQ8,subQ7,subQ6,subQ5,subQ4,subQ3,subQ2,subQ1,subQ0])],"isStart":true});Q6=makeQuery(id+"F14.opShell","OFFSET_FACE",FACE,{"disambiguationData":[OSD([subQ10,subQ9,subQ8,subQ7,subQ6,subQ5,subQ4,subQ3,subQ2,subQ1,subQ0]),TDD([makeQuery(id+"F12.opBoolean","MERGE",FACE,{"derivedFrom":[subQ11,makeQuery(id+"F7.opPattern","COPY",FACE,{"derivedFrom":subQ11,"instanceName":"1"}),makeQuery(id+"F8.opPattern","COPY",FACE,{"derivedFrom":subQ11,"instanceName":"1"}),makeQuery(id+"F9.opPattern","COPY",FACE,{"derivedFrom":subQ11,"instanceName":"1"}),makeQuery(id+"F10.opPattern","COPY",FACE,{"derivedFrom":subQ11,"instanceName":"1"}),makeQuery(id+"F11.opPattern","COPY",FACE,{"derivedFrom":subQ11,"instanceName":"1"})]})]),OD(8.0)]});}
            var Q7;
            {var subQ0=sQuery(id+"F5.wireOp",EDGE,"E35");Q7=makeQuery(id+"F14.opShell","OFFSET_FACE",FACE,{"disambiguationData":[OSD([subQ0]),TDD([makeQuery(id+"F10.opPattern","COPY",FACE,{"derivedFrom":makeQuery(id+"F6.boolean.opBoolean","COPY",FACE,{"derivedFrom":makeQuery(id+"F6.opExtrude","CAP_FACE",FACE,{"disambiguationData":[OSD([subQ0])],"isStart":false})}),"instanceName":"1"})])]});}
            var Q8;
            {var subQ0=sQuery(id+"F0.wireOp",EDGE,"E19");var subQ1=sQuery(id+"F0.wireOp",EDGE,"E18");var subQ2=sQuery(id+"F0.wireOp",EDGE,"E17");var subQ3=sQuery(id+"F0.wireOp",EDGE,"E16");var subQ4=sQuery(id+"F0.wireOp",EDGE,"E15");var subQ5=sQuery(id+"F0.wireOp",EDGE,"E14");var subQ6=sQuery(id+"F0.wireOp",EDGE,"E13");var subQ7=sQuery(id+"F0.wireOp",EDGE,"E12");var subQ8=sQuery(id+"F0.wireOp",EDGE,"E11.trimOffspring");var subQ9=sQuery(id+"F0.wireOp",EDGE,"E0.0");var subQ10=sQuery(id+"F0.wireOp",EDGE,"Ghvy13B3-qNFz-JgCi-f515-eY6BPN7KZuCC");var subQ11=makeQuery(id+"F2.opExtrude","CAP_FACE",FACE,{"disambiguationData":[OSD([subQ10,subQ9,subQ8,subQ7,subQ6,subQ5,subQ4,subQ3,subQ2,subQ1,subQ0])],"isStart":true});Q8=makeQuery(id+"F14.opShell","OFFSET_FACE",FACE,{"disambiguationData":[OSD([subQ10,subQ9,subQ8,subQ7,subQ6,subQ5,subQ4,subQ3,subQ2,subQ1,subQ0]),TDD([makeQuery(id+"F12.opBoolean","MERGE",FACE,{"derivedFrom":[subQ11,makeQuery(id+"F7.opPattern","COPY",FACE,{"derivedFrom":subQ11,"instanceName":"1"}),makeQuery(id+"F8.opPattern","COPY",FACE,{"derivedFrom":subQ11,"instanceName":"1"}),makeQuery(id+"F9.opPattern","COPY",FACE,{"derivedFrom":subQ11,"instanceName":"1"}),makeQuery(id+"F10.opPattern","COPY",FACE,{"derivedFrom":subQ11,"instanceName":"1"}),makeQuery(id+"F11.opPattern","COPY",FACE,{"derivedFrom":subQ11,"instanceName":"1"})]})]),OD(9.0)]});}
            var Q9;
            {var subQ0=sQuery(id+"F0.wireOp",EDGE,"E19");var subQ1=sQuery(id+"F0.wireOp",EDGE,"E18");var subQ2=sQuery(id+"F0.wireOp",EDGE,"E17");var subQ3=sQuery(id+"F0.wireOp",EDGE,"E16");var subQ4=sQuery(id+"F0.wireOp",EDGE,"E15");var subQ5=sQuery(id+"F0.wireOp",EDGE,"E14");var subQ6=sQuery(id+"F0.wireOp",EDGE,"E13");var subQ7=sQuery(id+"F0.wireOp",EDGE,"E12");var subQ8=sQuery(id+"F0.wireOp",EDGE,"E11.trimOffspring");var subQ9=sQuery(id+"F0.wireOp",EDGE,"E0.0");var subQ10=sQuery(id+"F0.wireOp",EDGE,"Ghvy13B3-qNFz-JgCi-f515-eY6BPN7KZuCC");var subQ11=makeQuery(id+"F2.opExtrude","CAP_FACE",FACE,{"disambiguationData":[OSD([subQ10,subQ9,subQ8,subQ7,subQ6,subQ5,subQ4,subQ3,subQ2,subQ1,subQ0])],"isStart":true});Q9=makeQuery(id+"F14.opShell","OFFSET_FACE",FACE,{"disambiguationData":[OSD([subQ10,subQ9,subQ8,subQ7,subQ6,subQ5,subQ4,subQ3,subQ2,subQ1,subQ0]),TDD([makeQuery(id+"F12.opBoolean","MERGE",FACE,{"derivedFrom":[subQ11,makeQuery(id+"F7.opPattern","COPY",FACE,{"derivedFrom":subQ11,"instanceName":"1"}),makeQuery(id+"F8.opPattern","COPY",FACE,{"derivedFrom":subQ11,"instanceName":"1"}),makeQuery(id+"F9.opPattern","COPY",FACE,{"derivedFrom":subQ11,"instanceName":"1"}),makeQuery(id+"F10.opPattern","COPY",FACE,{"derivedFrom":subQ11,"instanceName":"1"}),makeQuery(id+"F11.opPattern","COPY",FACE,{"derivedFrom":subQ11,"instanceName":"1"})]})]),OD(7.0)]});}
            var Q10;
            {var subQ0=sQuery(id+"F5.wireOp",EDGE,"E35");Q10=makeQuery(id+"F14.opShell","OFFSET_FACE",FACE,{"disambiguationData":[OSD([subQ0]),TDD([makeQuery(id+"F9.opPattern","COPY",FACE,{"derivedFrom":makeQuery(id+"F6.boolean.opBoolean","COPY",FACE,{"derivedFrom":makeQuery(id+"F6.opExtrude","CAP_FACE",FACE,{"disambiguationData":[OSD([subQ0])],"isStart":false})}),"instanceName":"1"})])]});}
            var Q11;
            {var subQ0=sQuery(id+"F0.wireOp",EDGE,"E19");var subQ1=sQuery(id+"F0.wireOp",EDGE,"E18");var subQ2=sQuery(id+"F0.wireOp",EDGE,"E17");var subQ3=sQuery(id+"F0.wireOp",EDGE,"E16");var subQ4=sQuery(id+"F0.wireOp",EDGE,"E15");var subQ5=sQuery(id+"F0.wireOp",EDGE,"E14");var subQ6=sQuery(id+"F0.wireOp",EDGE,"E13");var subQ7=sQuery(id+"F0.wireOp",EDGE,"E12");var subQ8=sQuery(id+"F0.wireOp",EDGE,"E11.trimOffspring");var subQ9=sQuery(id+"F0.wireOp",EDGE,"E0.0");var subQ10=sQuery(id+"F0.wireOp",EDGE,"Ghvy13B3-qNFz-JgCi-f515-eY6BPN7KZuCC");var subQ11=makeQuery(id+"F2.opExtrude","CAP_FACE",FACE,{"disambiguationData":[OSD([subQ10,subQ9,subQ8,subQ7,subQ6,subQ5,subQ4,subQ3,subQ2,subQ1,subQ0])],"isStart":true});Q11=makeQuery(id+"F14.opShell","OFFSET_FACE",FACE,{"disambiguationData":[OSD([subQ10,subQ9,subQ8,subQ7,subQ6,subQ5,subQ4,subQ3,subQ2,subQ1,subQ0]),TDD([makeQuery(id+"F12.opBoolean","MERGE",FACE,{"derivedFrom":[subQ11,makeQuery(id+"F7.opPattern","COPY",FACE,{"derivedFrom":subQ11,"instanceName":"1"}),makeQuery(id+"F8.opPattern","COPY",FACE,{"derivedFrom":subQ11,"instanceName":"1"}),makeQuery(id+"F9.opPattern","COPY",FACE,{"derivedFrom":subQ11,"instanceName":"1"}),makeQuery(id+"F10.opPattern","COPY",FACE,{"derivedFrom":subQ11,"instanceName":"1"}),makeQuery(id+"F11.opPattern","COPY",FACE,{"derivedFrom":subQ11,"instanceName":"1"})]})]),OD(6.0)]});}
            var Q12;
            {var subQ0=sQuery(id+"F0.wireOp",EDGE,"E19");var subQ1=sQuery(id+"F0.wireOp",EDGE,"E18");var subQ2=sQuery(id+"F0.wireOp",EDGE,"E17");var subQ3=sQuery(id+"F0.wireOp",EDGE,"E16");var subQ4=sQuery(id+"F0.wireOp",EDGE,"E15");var subQ5=sQuery(id+"F0.wireOp",EDGE,"E14");var subQ6=sQuery(id+"F0.wireOp",EDGE,"E13");var subQ7=sQuery(id+"F0.wireOp",EDGE,"E12");var subQ8=sQuery(id+"F0.wireOp",EDGE,"E11.trimOffspring");var subQ9=sQuery(id+"F0.wireOp",EDGE,"E0.0");var subQ10=sQuery(id+"F0.wireOp",EDGE,"Ghvy13B3-qNFz-JgCi-f515-eY6BPN7KZuCC");var subQ11=makeQuery(id+"F2.opExtrude","CAP_FACE",FACE,{"disambiguationData":[OSD([subQ10,subQ9,subQ8,subQ7,subQ6,subQ5,subQ4,subQ3,subQ2,subQ1,subQ0])],"isStart":true});Q12=makeQuery(id+"F14.opShell","OFFSET_FACE",FACE,{"disambiguationData":[OSD([subQ10,subQ9,subQ8,subQ7,subQ6,subQ5,subQ4,subQ3,subQ2,subQ1,subQ0]),TDD([makeQuery(id+"F12.opBoolean","MERGE",FACE,{"derivedFrom":[subQ11,makeQuery(id+"F7.opPattern","COPY",FACE,{"derivedFrom":subQ11,"instanceName":"1"}),makeQuery(id+"F8.opPattern","COPY",FACE,{"derivedFrom":subQ11,"instanceName":"1"}),makeQuery(id+"F9.opPattern","COPY",FACE,{"derivedFrom":subQ11,"instanceName":"1"}),makeQuery(id+"F10.opPattern","COPY",FACE,{"derivedFrom":subQ11,"instanceName":"1"}),makeQuery(id+"F11.opPattern","COPY",FACE,{"derivedFrom":subQ11,"instanceName":"1"})]})]),OD(4.0)]});}
            var Q13;
            {var subQ0=sQuery(id+"F5.wireOp",EDGE,"E35");Q13=makeQuery(id+"F14.opShell","OFFSET_FACE",FACE,{"disambiguationData":[OSD([subQ0]),TDD([makeQuery(id+"F8.opPattern","COPY",FACE,{"derivedFrom":makeQuery(id+"F6.boolean.opBoolean","COPY",FACE,{"derivedFrom":makeQuery(id+"F6.opExtrude","CAP_FACE",FACE,{"disambiguationData":[OSD([subQ0])],"isStart":false})}),"instanceName":"1"})])]});}
            var Q14;
            {var subQ0=sQuery(id+"F0.wireOp",EDGE,"E19");var subQ1=sQuery(id+"F0.wireOp",EDGE,"E18");var subQ2=sQuery(id+"F0.wireOp",EDGE,"E17");var subQ3=sQuery(id+"F0.wireOp",EDGE,"E16");var subQ4=sQuery(id+"F0.wireOp",EDGE,"E15");var subQ5=sQuery(id+"F0.wireOp",EDGE,"E14");var subQ6=sQuery(id+"F0.wireOp",EDGE,"E13");var subQ7=sQuery(id+"F0.wireOp",EDGE,"E12");var subQ8=sQuery(id+"F0.wireOp",EDGE,"E11.trimOffspring");var subQ9=sQuery(id+"F0.wireOp",EDGE,"E0.0");var subQ10=sQuery(id+"F0.wireOp",EDGE,"Ghvy13B3-qNFz-JgCi-f515-eY6BPN7KZuCC");var subQ11=makeQuery(id+"F2.opExtrude","CAP_FACE",FACE,{"disambiguationData":[OSD([subQ10,subQ9,subQ8,subQ7,subQ6,subQ5,subQ4,subQ3,subQ2,subQ1,subQ0])],"isStart":true});Q14=makeQuery(id+"F14.opShell","OFFSET_FACE",FACE,{"disambiguationData":[OSD([subQ10,subQ9,subQ8,subQ7,subQ6,subQ5,subQ4,subQ3,subQ2,subQ1,subQ0]),TDD([makeQuery(id+"F12.opBoolean","MERGE",FACE,{"derivedFrom":[subQ11,makeQuery(id+"F7.opPattern","COPY",FACE,{"derivedFrom":subQ11,"instanceName":"1"}),makeQuery(id+"F8.opPattern","COPY",FACE,{"derivedFrom":subQ11,"instanceName":"1"}),makeQuery(id+"F9.opPattern","COPY",FACE,{"derivedFrom":subQ11,"instanceName":"1"}),makeQuery(id+"F10.opPattern","COPY",FACE,{"derivedFrom":subQ11,"instanceName":"1"}),makeQuery(id+"F11.opPattern","COPY",FACE,{"derivedFrom":subQ11,"instanceName":"1"})]})]),OD(5.0)]});}
            var Q15;
            {var subQ0=sQuery(id+"F0.wireOp",EDGE,"E19");var subQ1=sQuery(id+"F0.wireOp",EDGE,"E18");var subQ2=sQuery(id+"F0.wireOp",EDGE,"E17");var subQ3=sQuery(id+"F0.wireOp",EDGE,"E16");var subQ4=sQuery(id+"F0.wireOp",EDGE,"E15");var subQ5=sQuery(id+"F0.wireOp",EDGE,"E14");var subQ6=sQuery(id+"F0.wireOp",EDGE,"E13");var subQ7=sQuery(id+"F0.wireOp",EDGE,"E12");var subQ8=sQuery(id+"F0.wireOp",EDGE,"E11.trimOffspring");var subQ9=sQuery(id+"F0.wireOp",EDGE,"E0.0");var subQ10=sQuery(id+"F0.wireOp",EDGE,"Ghvy13B3-qNFz-JgCi-f515-eY6BPN7KZuCC");var subQ11=makeQuery(id+"F2.opExtrude","CAP_FACE",FACE,{"disambiguationData":[OSD([subQ10,subQ9,subQ8,subQ7,subQ6,subQ5,subQ4,subQ3,subQ2,subQ1,subQ0])],"isStart":true});Q15=makeQuery(id+"F14.opShell","OFFSET_FACE",FACE,{"disambiguationData":[OSD([subQ10,subQ9,subQ8,subQ7,subQ6,subQ5,subQ4,subQ3,subQ2,subQ1,subQ0]),TDD([makeQuery(id+"F12.opBoolean","MERGE",FACE,{"derivedFrom":[subQ11,makeQuery(id+"F7.opPattern","COPY",FACE,{"derivedFrom":subQ11,"instanceName":"1"}),makeQuery(id+"F8.opPattern","COPY",FACE,{"derivedFrom":subQ11,"instanceName":"1"}),makeQuery(id+"F9.opPattern","COPY",FACE,{"derivedFrom":subQ11,"instanceName":"1"}),makeQuery(id+"F10.opPattern","COPY",FACE,{"derivedFrom":subQ11,"instanceName":"1"}),makeQuery(id+"F11.opPattern","COPY",FACE,{"derivedFrom":subQ11,"instanceName":"1"})]})]),OD(2.0)]});}
            var Q16;
            {var subQ0=sQuery(id+"F5.wireOp",EDGE,"E35");Q16=makeQuery(id+"F14.opShell","OFFSET_FACE",FACE,{"disambiguationData":[OSD([subQ0]),TDD([makeQuery(id+"F7.opPattern","COPY",FACE,{"derivedFrom":makeQuery(id+"F6.boolean.opBoolean","COPY",FACE,{"derivedFrom":makeQuery(id+"F6.opExtrude","CAP_FACE",FACE,{"disambiguationData":[OSD([subQ0])],"isStart":false})}),"instanceName":"1"})])]});}
            var Q17;
            {var subQ0=sQuery(id+"F0.wireOp",EDGE,"E19");var subQ1=sQuery(id+"F0.wireOp",EDGE,"E18");var subQ2=sQuery(id+"F0.wireOp",EDGE,"E17");var subQ3=sQuery(id+"F0.wireOp",EDGE,"E16");var subQ4=sQuery(id+"F0.wireOp",EDGE,"E15");var subQ5=sQuery(id+"F0.wireOp",EDGE,"E14");var subQ6=sQuery(id+"F0.wireOp",EDGE,"E13");var subQ7=sQuery(id+"F0.wireOp",EDGE,"E12");var subQ8=sQuery(id+"F0.wireOp",EDGE,"E11.trimOffspring");var subQ9=sQuery(id+"F0.wireOp",EDGE,"E0.0");var subQ10=sQuery(id+"F0.wireOp",EDGE,"Ghvy13B3-qNFz-JgCi-f515-eY6BPN7KZuCC");var subQ11=makeQuery(id+"F2.opExtrude","CAP_FACE",FACE,{"disambiguationData":[OSD([subQ10,subQ9,subQ8,subQ7,subQ6,subQ5,subQ4,subQ3,subQ2,subQ1,subQ0])],"isStart":true});Q17=makeQuery(id+"F14.opShell","OFFSET_FACE",FACE,{"disambiguationData":[OSD([subQ10,subQ9,subQ8,subQ7,subQ6,subQ5,subQ4,subQ3,subQ2,subQ1,subQ0]),TDD([makeQuery(id+"F12.opBoolean","MERGE",FACE,{"derivedFrom":[subQ11,makeQuery(id+"F7.opPattern","COPY",FACE,{"derivedFrom":subQ11,"instanceName":"1"}),makeQuery(id+"F8.opPattern","COPY",FACE,{"derivedFrom":subQ11,"instanceName":"1"}),makeQuery(id+"F9.opPattern","COPY",FACE,{"derivedFrom":subQ11,"instanceName":"1"}),makeQuery(id+"F10.opPattern","COPY",FACE,{"derivedFrom":subQ11,"instanceName":"1"}),makeQuery(id+"F11.opPattern","COPY",FACE,{"derivedFrom":subQ11,"instanceName":"1"})]})]),OD(3.0)]});}
            var Q18;
            {var subQ0=makeQuery(id+"F2.opExtrude","CAP_FACE",FACE,{"disambiguationData":[OSD([sQuery(id+"F0.wireOp",EDGE,"Ghvy13B3-qNFz-JgCi-f515-eY6BPN7KZuCC"),sQuery(id+"F0.wireOp",EDGE,"E0.0"),sQuery(id+"F0.wireOp",EDGE,"E11.trimOffspring"),sQuery(id+"F0.wireOp",EDGE,"E12"),sQuery(id+"F0.wireOp",EDGE,"E13"),sQuery(id+"F0.wireOp",EDGE,"E14"),sQuery(id+"F0.wireOp",EDGE,"E15"),sQuery(id+"F0.wireOp",EDGE,"E16"),sQuery(id+"F0.wireOp",EDGE,"E17"),sQuery(id+"F0.wireOp",EDGE,"E18"),sQuery(id+"F0.wireOp",EDGE,"E19")])],"isStart":false});Q18=makeQuery(id+"F12.opBoolean","MERGE",FACE,{"derivedFrom":[subQ0,makeQuery(id+"F7.opPattern","COPY",FACE,{"derivedFrom":subQ0,"instanceName":"1"}),makeQuery(id+"F8.opPattern","COPY",FACE,{"derivedFrom":subQ0,"instanceName":"1"}),makeQuery(id+"F9.opPattern","COPY",FACE,{"derivedFrom":subQ0,"instanceName":"1"}),makeQuery(id+"F10.opPattern","COPY",FACE,{"derivedFrom":subQ0,"instanceName":"1"}),makeQuery(id+"F11.opPattern","COPY",FACE,{"derivedFrom":subQ0,"instanceName":"1"})]});}
            extrude(context, id + "F15", {"entities" : qUnion([Q0, Q1, Q2, Q3, Q4, Q5, Q6, Q7, Q8, Q9, Q10, Q11, Q12, Q13, Q14, Q15, Q16, Q17]), "operationType" : NewBodyOperationType.ADD, "endBound" : BoundingType.UP_TO_SURFACE, "endBoundEntityFace" : qUnion([Q18]), "depth" : 25 * mm});
        }
    });
